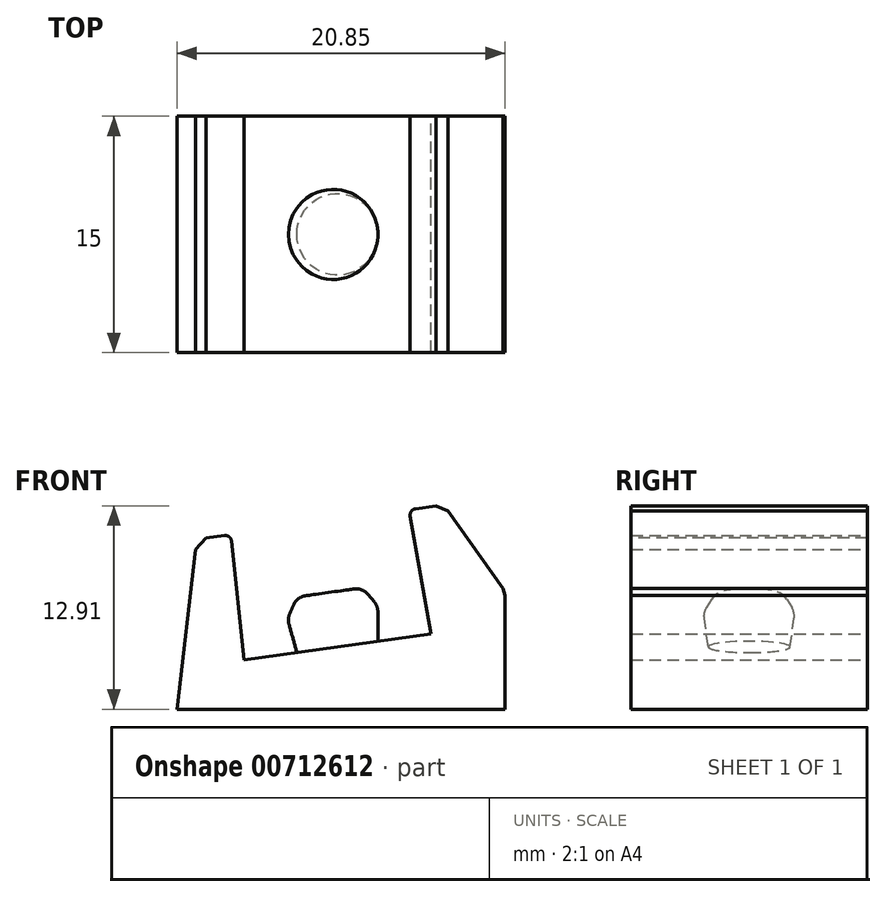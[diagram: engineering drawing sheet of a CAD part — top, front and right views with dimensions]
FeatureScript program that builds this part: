
annotation { "Feature Type Name" : "Feature", "Feature Type Description" : "" }
export const myFeature = defineFeature(function(context is Context, id is Id, definition is map)
    precondition{}
    {
        {
            var Q0;
            Q0=qCreatedBy(makeId("Front.planeOp"),FACE);
            var sketch = newSketch(context, id + "F0", { "sketchPlane" : qUnion([Q0])});
            skLineSegment(sketch, "E0", {"start": v(-10.65, -2.5) * mm, "end": v(10, -5.4) * mm});
            skLineSegment(sketch, "E1", {"start": v(7.92, 8) * mm, "end": v(6.12, 8) * mm});
            skLineSegment(sketch, "E2", {"start": v(5.73, 7.6) * mm, "end": v(6, 0) * mm});
            skLineSegment(sketch, "E3", {"start": v(6, 0) * mm, "end": v(-6, 0) * mm});
            skLineSegment(sketch, "E4", {"start": v(-6, 0) * mm, "end": v(-5.73, 7.6) * mm});
            skLineSegment(sketch, "E5", {"start": v(-6.12, 8) * mm, "end": v(-7.92, 8) * mm});
            skLineSegment(sketch, "E6", {"start": v(-7.92, 8) * mm, "end": v(-10.65, -2.5) * mm});
            skPoint(sketch, "E7.visualSharp", {"position": v(-5.72, 8) * mm});
            skArc(sketch, "E7.filletArc", {"start": v(-5.73, 7.6) * mm, "mid": v(-5.84, 7.88) * mm, "end": v(-6.12, 8) * mm});
            skPoint(sketch, "E8.visualSharp", {"position": v(5.72, 8) * mm});
            skArc(sketch, "E8.filletArc", {"start": v(6.12, 8) * mm, "mid": v(5.84, 7.88) * mm, "end": v(5.73, 7.6) * mm});
            skLineSegment(sketch, "E9", {"start": v(10, -12.66) * mm, "end": v(10, -7.3) * mm, "construction": true});
            skPoint(sketch, "E10", {"position": v(10, 0) * mm});
            skLineSegment(sketch, "E11", {"start": v(-10, 9.32) * mm, "end": v(-10, -7.3) * mm, "construction": true});
            skPoint(sketch, "E12", {"position": v(-10, 0) * mm});
            skLineSegment(sketch, "E13", {"start": v(-16.66, 2) * mm, "end": v(15.33, 2) * mm, "construction": true});
            skLineSegment(sketch, "E14", {"start": v(7.92, 8) * mm, "end": v(11.04, 2) * mm});
            skLineSegment(sketch, "E15", {"start": v(11.04, 2) * mm, "end": v(10, -5.4) * mm});
            skSolve(sketch);
        }
        {
            var Q0;
            Q0 = qSketchRegion(id + "F0", true);
            extrude(context, id + "F1", {"entities" : qUnion([Q0]), "endBound" : BoundingType.SYMMETRIC, "depth" : 15 * mm, "offsetDistance" : 25.4 * mm});
        }
        {
            var Q0;
            Q0=qCreatedBy(makeId("Front.planeOp"),FACE);
            var sketch = newSketch(context, id + "F2", { "sketchPlane" : qUnion([Q0])});
            skLineSegment(sketch, "E16", {"start": v(0, 0) * mm, "end": v(0, 3.5) * mm});
            skLineSegment(sketch, "E17", {"start": v(0, 3.5) * mm, "end": v(-1.54, 3.5) * mm});
            skLineSegment(sketch, "E18", {"start": v(-2.6, 0) * mm, "end": v(0, 0) * mm});
            skLineSegment(sketch, "E19", {"start": v(-2.85, 1.85) * mm, "end": v(-2.6, 0) * mm});
            skLineSegment(sketch, "E20", {"start": v(-2.71, 2.5) * mm, "end": v(-2.4, 3.02) * mm});
            skPoint(sketch, "E21.visualSharp", {"position": v(-2.9, 2.2) * mm});
            skArc(sketch, "E21.filletArc", {"start": v(-2.71, 2.5) * mm, "mid": v(-2.84, 2.19) * mm, "end": v(-2.85, 1.85) * mm});
            skPoint(sketch, "E22.visualSharp", {"position": v(-2.1, 3.5) * mm});
            skArc(sketch, "E22.filletArc", {"start": v(-1.54, 3.5) * mm, "mid": v(-2.03, 3.37) * mm, "end": v(-2.4, 3.02) * mm});
            skSolve(sketch);
        }
        {
            var Q0;
            Q0 = qSketchRegion(id + "F2", true);
            var Q1;
            Q1=sQuery(id+"F2.wireOp",EDGE,"E16");
            revolve(context, id + "F3", {"operationType" : NewBodyOperationType.ADD, "surfaceOperationType" : NewSurfaceOperationType.NEW, "entities" : qUnion([Q0]), "axis" : qUnion([Q1]), "revolveType" : RevolveType.FULL});
        }
        {
            var Q0;
            Q0=makeQuery(id+"F1.opExtrude","SWEPT_EDGE",EDGE,{"disambiguationData":[OSD([sQuery(id+"F0.wireOp",EDGE,"07fc189b-04c7-4121-a5a2-7e96203b3d35"),sQuery(id+"F0.wireOp",EDGE,"E1")])]});
            var Q1;
            Q1=makeQuery(id+"F1.opExtrude","SWEPT_EDGE",EDGE,{"disambiguationData":[OSD([sQuery(id+"F0.wireOp",EDGE,"E1"),sQuery(id+"F0.wireOp",EDGE,"E8.filletArc")])]});
            var Q2;
            Q2=makeQuery(id+"F1.opExtrude","SWEPT_EDGE",EDGE,{"disambiguationData":[OSD([sQuery(id+"F0.wireOp",EDGE,"E2"),sQuery(id+"F0.wireOp",EDGE,"E8.filletArc")])]});
            var Q3;
            Q3=makeQuery(id+"F1.opExtrude","SWEPT_EDGE",EDGE,{"disambiguationData":[OSD([sQuery(id+"F0.wireOp",EDGE,"E4"),sQuery(id+"F0.wireOp",EDGE,"E7.filletArc")])]});
            var Q4;
            Q4=makeQuery(id+"F1.opExtrude","SWEPT_EDGE",EDGE,{"disambiguationData":[OSD([sQuery(id+"F0.wireOp",EDGE,"E5"),sQuery(id+"F0.wireOp",EDGE,"E7.filletArc")])]});
            var Q5;
            Q5=makeQuery(id+"F1.opExtrude","SWEPT_EDGE",EDGE,{"disambiguationData":[OSD([sQuery(id+"F0.wireOp",EDGE,"E5"),sQuery(id+"F0.wireOp",EDGE,"E6")])]});
            var Q6;
            Q6=makeQuery(id+"F1.opExtrude","SWEPT_EDGE",EDGE,{"disambiguationData":[OSD([sQuery(id+"F0.wireOp",EDGE,"E14"),sQuery(id+"F0.wireOp",EDGE,"E15")])]});
            chamfer(context, id + "F4", {"entities" : qUnion([Q0, Q1, Q2, Q3, Q4, Q5, Q6]), "width" : 0.8 * mm, "tangentPropagation" : true});
        }
        {
            var Q0;
            Q0=makeQuery(id+"F1.opExtrude","SWEPT_BODY",BODY,{"disambiguationData":[OSD([sQuery(id+"F0.wireOp",EDGE,"E0"),sQuery(id+"F0.wireOp",EDGE,"E1"),sQuery(id+"F0.wireOp",EDGE,"E2"),sQuery(id+"F0.wireOp",EDGE,"E3"),sQuery(id+"F0.wireOp",EDGE,"E4"),sQuery(id+"F0.wireOp",EDGE,"E5"),sQuery(id+"F0.wireOp",EDGE,"E6"),sQuery(id+"F0.wireOp",EDGE,"E7.filletArc"),sQuery(id+"F0.wireOp",EDGE,"E8.filletArc"),sQuery(id+"F0.wireOp",EDGE,"E14"),sQuery(id+"F0.wireOp",EDGE,"E15")])]});
            var Q1;
            Q1=makeQuery(id+"F1.opExtrude","SWEPT_EDGE",EDGE,{"disambiguationData":[OSD([sQuery(id+"F0.wireOp",EDGE,"E0"),sQuery(id+"F0.wireOp",EDGE,"E6")])]});
            transform(context, id + "F5", {"entities" : qUnion([Q0]), "transformType" : TransformType.ROTATION, "transformAxis" : qUnion([Q1]), "angle" : 8 * degree, "oppositeDirection" : true, "makeCopy" : false});
        }
    });
